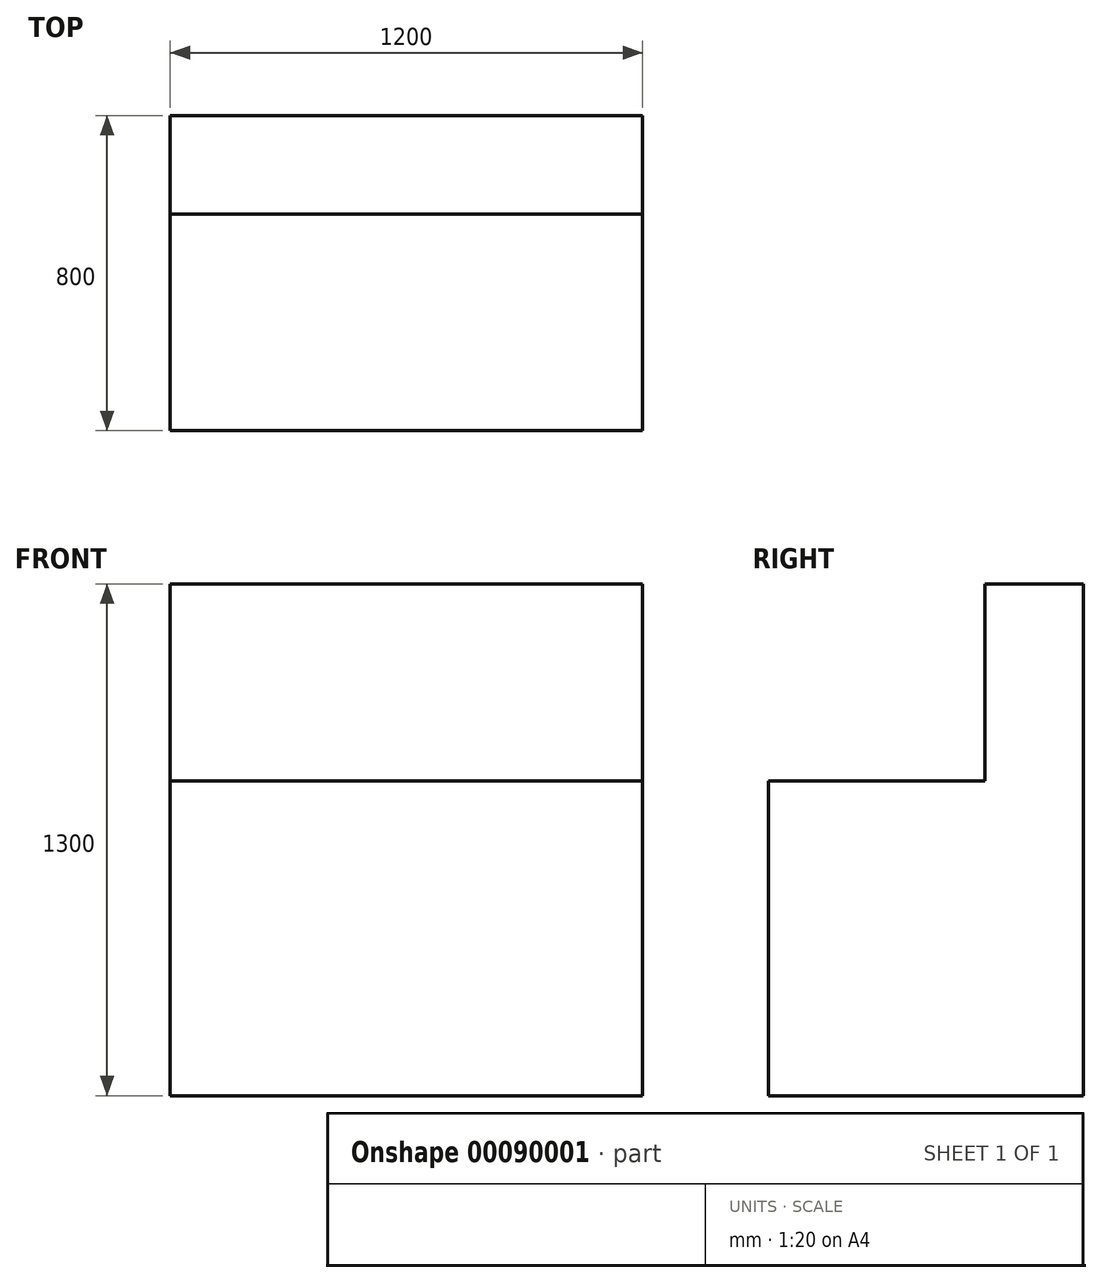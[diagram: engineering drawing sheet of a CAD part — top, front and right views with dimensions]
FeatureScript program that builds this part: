
annotation { "Feature Type Name" : "Feature", "Feature Type Description" : "" }
export const myFeature = defineFeature(function(context is Context, id is Id, definition is map)
    precondition{}
    {
        {
            var Q0;
            Q0=qCreatedBy(makeId("Top.planeOp"),FACE);
            var sketch = newSketch(context, id + "F0", { "sketchPlane" : qUnion([Q0])});
            skLineSegment(sketch, "E0.bottom", {"start": v(0, 0) * mm, "end": v(1200, 0) * mm});
            skLineSegment(sketch, "E0.top", {"start": v(0, 800) * mm, "end": v(1200, 800) * mm});
            skLineSegment(sketch, "E0.left", {"start": v(0, 0) * mm, "end": v(0, 800) * mm});
            skLineSegment(sketch, "E0.right", {"start": v(1200, 0) * mm, "end": v(1200, 800) * mm});
            skSolve(sketch);
        }
        {
            var Q0;
            Q0 = qSketchRegion(id + "F0", true);
            extrude(context, id + "F1", {"entities" : qUnion([Q0]), "depth" : 800 * mm});
        }
        {
            var Q0;
            Q0=makeQuery(id+"F1.opExtrude","CAP_FACE",FACE,{"disambiguationData":[OSD([sQuery(id+"F0.wireOp",EDGE,"E0.bottom"),sQuery(id+"F0.wireOp",EDGE,"E0.top"),sQuery(id+"F0.wireOp",EDGE,"E0.left"),sQuery(id+"F0.wireOp",EDGE,"E0.right")])],"isStart":false});
            var sketch = newSketch(context, id + "F2", { "sketchPlane" : qUnion([Q0])});
            skLineSegment(sketch, "E1.bottom", {"start": v(0, 800) * mm, "end": v(1200, 800) * mm});
            skLineSegment(sketch, "E1.top", {"start": v(0, 550) * mm, "end": v(1200, 550) * mm});
            skLineSegment(sketch, "E1.left", {"start": v(0, 800) * mm, "end": v(0, 550) * mm});
            skLineSegment(sketch, "E1.right", {"start": v(1200, 800) * mm, "end": v(1200, 550) * mm});
            skSolve(sketch);
        }
        {
            var Q0;
            Q0 = qSketchRegion(id + "F2", true);
            var Q1;
            Q1=makeQuery(id+"F2.imprint","IMPRINT",FACE,{"disambiguationData":[TD([[makeQuery(id+"F2.imprint","IMPRINT",EDGE,{"derivedFrom":sQuery(id+"F2.wireOp",EDGE,"E1.bottom")}),-1.0]])]});
            extrude(context, id + "F3", {"entities" : qUnion([Q0, Q1]), "operationType" : NewBodyOperationType.ADD, "depth" : 500 * mm});
        }
    });
